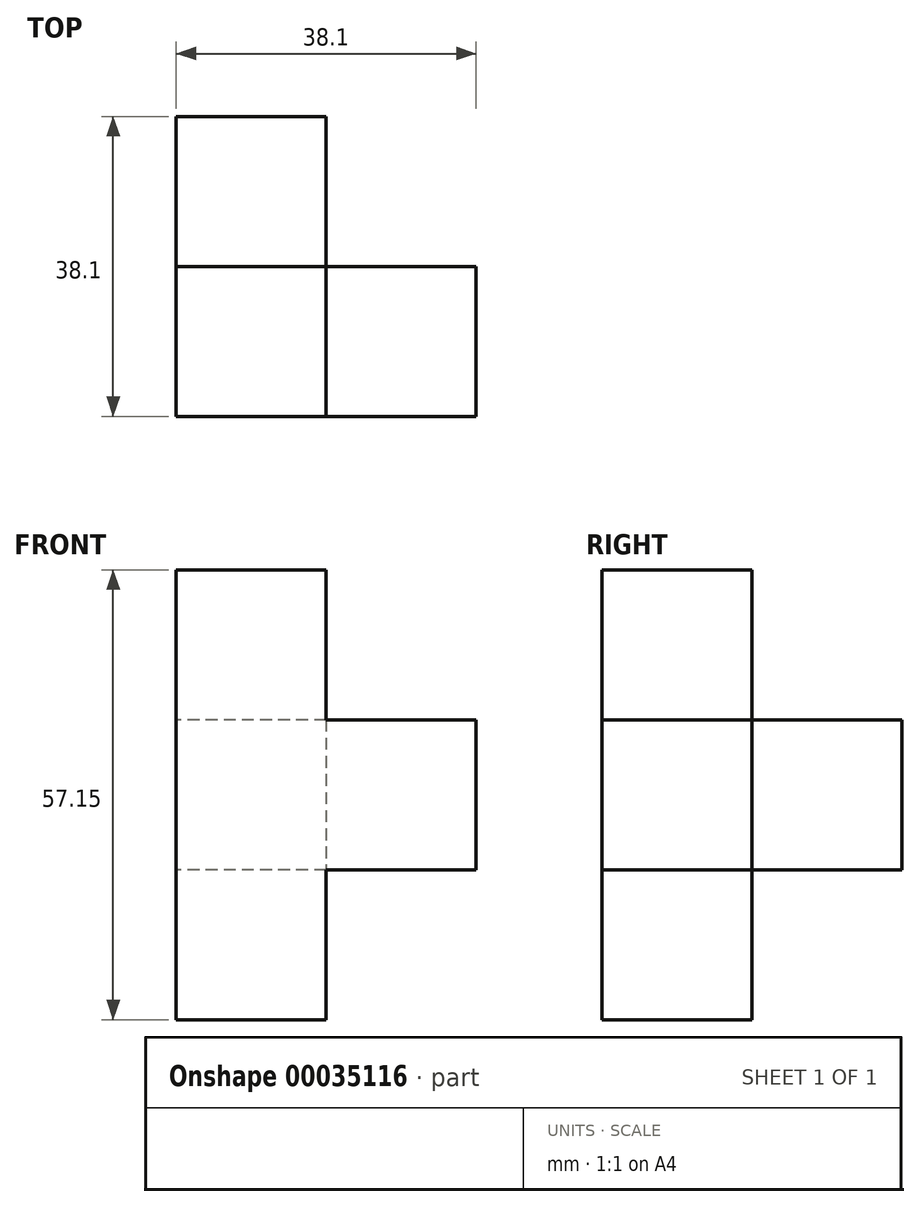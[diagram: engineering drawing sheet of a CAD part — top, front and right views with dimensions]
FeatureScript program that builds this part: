
annotation { "Feature Type Name" : "Feature", "Feature Type Description" : "" }
export const myFeature = defineFeature(function(context is Context, id is Id, definition is map)
    precondition{}
    {
        {
            var Q0;
            Q0=qCreatedBy(makeId("Top.planeOp"),FACE);
            var sketch = newSketch(context, id + "F0", { "sketchPlane" : qUnion([Q0])});
            skLineSegment(sketch, "E0.bottom", {"start": v(0, 0) * mm, "end": v(19.05, 0) * mm});
            skLineSegment(sketch, "E0.top", {"start": v(0, 19.05) * mm, "end": v(19.05, 19.05) * mm});
            skLineSegment(sketch, "E0.left", {"start": v(0, 0) * mm, "end": v(0, 19.05) * mm});
            skLineSegment(sketch, "E0.right", {"start": v(19.05, 0) * mm, "end": v(19.05, 19.05) * mm});
            skSolve(sketch);
        }
        {
            var Q0;
            Q0 = qSketchRegion(id + "F0", true);
            extrude(context, id + "F1", {"entities" : qUnion([Q0]), "depth" : 57.15 * mm});
        }
        {
            var Q0;
            Q0=makeQuery(id+"F1.opExtrude","SWEPT_FACE",FACE,{"disambiguationData":[OSD([sQuery(id+"F0.wireOp",EDGE,"E0.right")])]});
            var sketch = newSketch(context, id + "F2", { "sketchPlane" : qUnion([Q0])});
            skLineSegment(sketch, "E1.bottom", {"start": v(0, 57.15) * mm, "end": v(19.05, 57.15) * mm});
            skLineSegment(sketch, "E1.top", {"start": v(0, 19.05) * mm, "end": v(19.05, 19.05) * mm});
            skLineSegment(sketch, "E1.left", {"start": v(0, 57.15) * mm, "end": v(0, 19.05) * mm});
            skLineSegment(sketch, "E1.right", {"start": v(19.05, 57.15) * mm, "end": v(19.05, 19.05) * mm});
            skLineSegment(sketch, "E2.top", {"start": v(0, 38.1) * mm, "end": v(19.05, 38.1) * mm});
            skLineSegment(sketch, "E2.left", {"start": v(0, 19.05) * mm, "end": v(0, 38.1) * mm});
            skLineSegment(sketch, "E2.right", {"start": v(19.05, 19.05) * mm, "end": v(19.05, 38.1) * mm});
            skSolve(sketch);
        }
        {
            var Q0;
            Q0=makeQuery(id+"F2.imprint","IMPRINT",FACE,{"disambiguationData":[TD([[makeQuery(id+"F2.imprint","IMPRINT",EDGE,{"derivedFrom":sQuery(id+"F2.wireOp",EDGE,"E1.top")}),1.0]])]});
            extrude(context, id + "F3", {"entities" : qUnion([Q0]), "operationType" : NewBodyOperationType.ADD, "depth" : 19.05 * mm});
        }
        {
            var Q0;
            Q0=makeQuery(id+"F3.boolean.opBoolean","MERGE",FACE,{"derivedFrom":[makeQuery(id+"F1.opExtrude","SWEPT_FACE",FACE,{"disambiguationData":[OSD([sQuery(id+"F0.wireOp",EDGE,"E0.top")])]}),makeQuery(id+"F3.opExtrude","SWEPT_FACE",FACE,{"disambiguationData":[OSD([sQuery(id+"F2.wireOp",EDGE,"E2.right")])]})]});
            var sketch = newSketch(context, id + "F4", { "sketchPlane" : qUnion([Q0])});
            skLineSegment(sketch, "E3.bottom", {"start": v(-19.05, 38.1) * mm, "end": v(0, 38.1) * mm});
            skLineSegment(sketch, "E3.top", {"start": v(-19.05, 19.05) * mm, "end": v(0, 19.05) * mm});
            skLineSegment(sketch, "E3.left", {"start": v(-19.05, 38.1) * mm, "end": v(-19.05, 19.05) * mm});
            skLineSegment(sketch, "E3.right", {"start": v(0, 38.1) * mm, "end": v(0, 19.05) * mm});
            skSolve(sketch);
        }
        {
            var Q0;
            Q0 = qSketchRegion(id + "F4", true);
            extrude(context, id + "F5", {"entities" : qUnion([Q0]), "operationType" : NewBodyOperationType.ADD, "depth" : 19.05 * mm});
        }
    });
